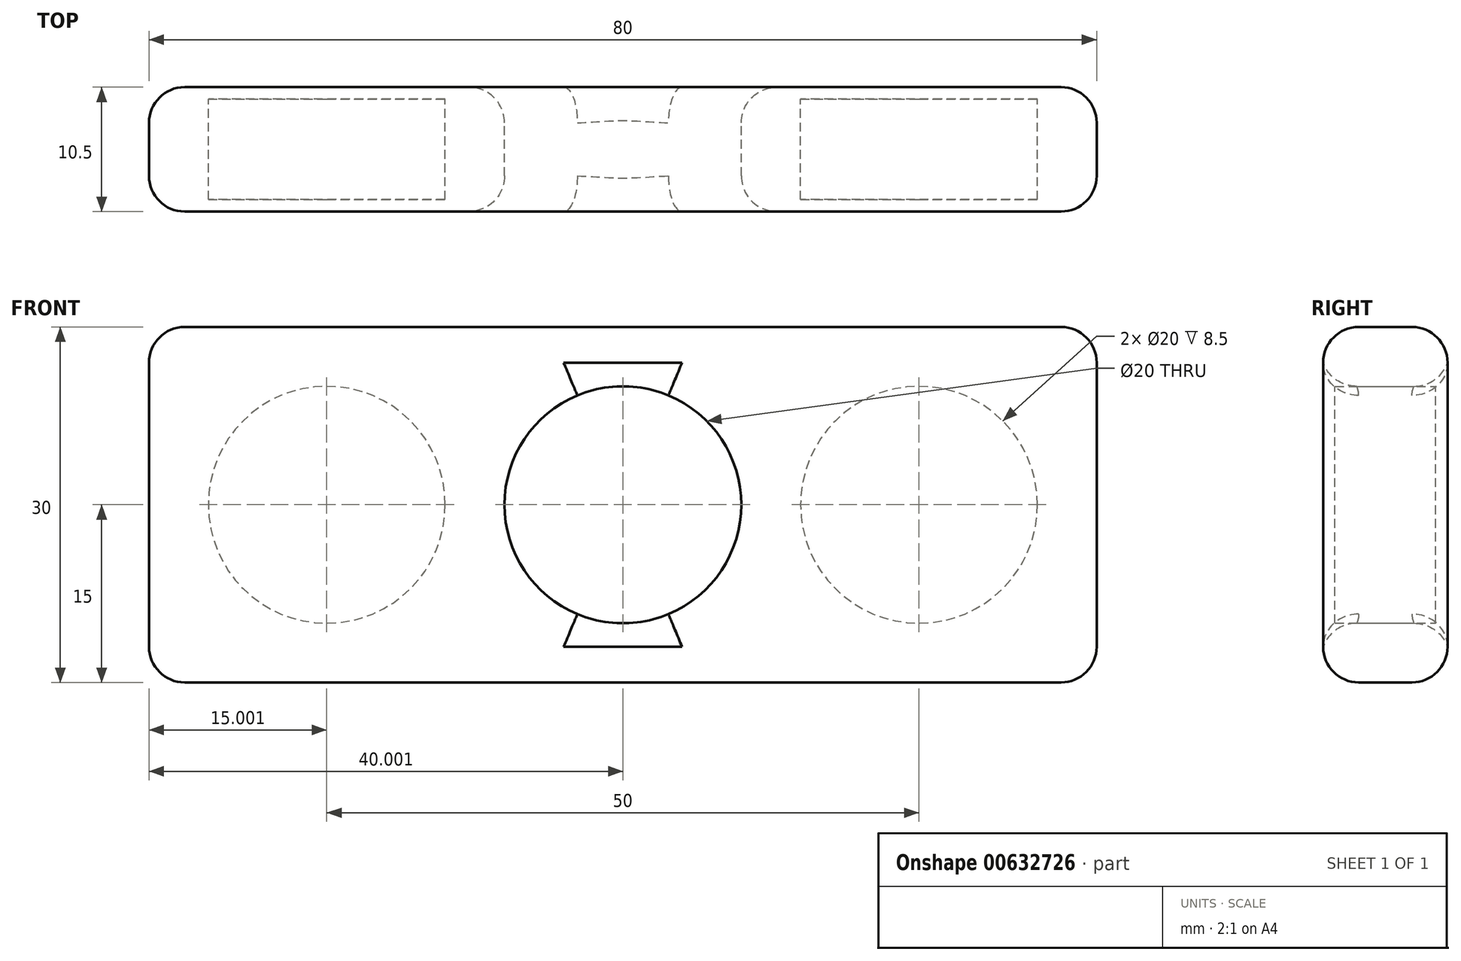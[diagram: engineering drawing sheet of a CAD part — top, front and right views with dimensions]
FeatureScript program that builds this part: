
annotation { "Feature Type Name" : "Feature", "Feature Type Description" : "" }
export const myFeature = defineFeature(function(context is Context, id is Id, definition is map)
    precondition{}
    {
        {
            var Q0;
            Q0=qCreatedBy(makeId("Front.planeOp"),FACE);
            var sketch = newSketch(context, id + "F0", { "sketchPlane" : qUnion([Q0])});
            skLineSegment(sketch, "E0.bottom", {"start": v(-23.99, 15) * mm, "end": v(-103.99, 15) * mm});
            skLineSegment(sketch, "E0.top", {"start": v(-23.99, -15) * mm, "end": v(-103.99, -15) * mm});
            skLineSegment(sketch, "E0.left", {"start": v(-23.99, 15) * mm, "end": v(-23.99, -15) * mm});
            skLineSegment(sketch, "E0.right", {"start": v(-103.99, 15) * mm, "end": v(-103.99, -15) * mm});
            skPoint(sketch, "E0.middle", {"position": v(-63.99, 0) * mm});
            skCircle(sketch, "E1", {"center": v(-63.99, 0) * mm, "radius": 10 * mm});
            skPoint(sketch, "E2.endSnap0", {"position": v(-103.99, 0) * mm});
            skCircle(sketch, "E3", {"center": v(-88.99, 0) * mm, "radius": 10 * mm});
            skCircle(sketch, "E4", {"center": v(-38.99, 0) * mm, "radius": 10 * mm});
            skSolve(sketch);
        }
        {
            var Q0;
            Q0 = qSketchRegion(id + "F0", true);
            extrude(context, id + "F1", {"entities" : qUnion([Q0]), "depth" : 8.5 * mm, "offsetDistance" : 25.4 * mm});
        }
        {
            var Q0;
            Q0=makeQuery(id+"F1.opExtrude","CAP_FACE",FACE,{"disambiguationData":[OSD([sQuery(id+"F0.wireOp",EDGE,"E0.bottom"),sQuery(id+"F0.wireOp",EDGE,"E0.top"),sQuery(id+"F0.wireOp",EDGE,"E0.left"),sQuery(id+"F0.wireOp",EDGE,"E0.right"),sQuery(id+"F0.wireOp",EDGE,"E1"),sQuery(id+"F0.wireOp",EDGE,"E3"),sQuery(id+"F0.wireOp",EDGE,"E4")])],"isStart":false});
            var sketch = newSketch(context, id + "F2", { "sketchPlane" : qUnion([Q0])});
            skLineSegment(sketch, "E5.0", {"start": v(-23.99, 15) * mm, "end": v(-103.99, 15) * mm});
            skLineSegment(sketch, "E6.0", {"start": v(-103.99, 15) * mm, "end": v(-103.99, -15) * mm});
            skLineSegment(sketch, "E7.0", {"start": v(-23.99, -15) * mm, "end": v(-103.99, -15) * mm});
            skLineSegment(sketch, "E8.0", {"start": v(-23.99, 15) * mm, "end": v(-23.99, -15) * mm});
            skCircle(sketch, "E9.0", {"center": v(-63.99, 0) * mm, "radius": 10 * mm});
            skSolve(sketch);
        }
        {
            var Q0;
            Q0 = qSketchRegion(id + "F2", true);
            extrude(context, id + "F3", {"entities" : qUnion([Q0]), "operationType" : NewBodyOperationType.ADD, "depth" : 1 * mm, "offsetDistance" : 25.4 * mm});
        }
        {
            var Q0;
            Q0=makeQuery(id+"F1.opExtrude","CAP_FACE",FACE,{"disambiguationData":[OSD([sQuery(id+"F0.wireOp",EDGE,"E0.bottom"),sQuery(id+"F0.wireOp",EDGE,"E0.top"),sQuery(id+"F0.wireOp",EDGE,"E0.left"),sQuery(id+"F0.wireOp",EDGE,"E0.right"),sQuery(id+"F0.wireOp",EDGE,"E1"),sQuery(id+"F0.wireOp",EDGE,"E3"),sQuery(id+"F0.wireOp",EDGE,"E4")])],"isStart":true});
            var sketch = newSketch(context, id + "F4", { "sketchPlane" : qUnion([Q0])});
            skLineSegment(sketch, "E10.0", {"start": v(23.99, 15) * mm, "end": v(103.99, 15) * mm});
            skLineSegment(sketch, "E11.0", {"start": v(23.99, 15) * mm, "end": v(23.99, -15) * mm});
            skLineSegment(sketch, "E12.0", {"start": v(23.99, -15) * mm, "end": v(103.99, -15) * mm});
            skLineSegment(sketch, "E13.0", {"start": v(103.99, 15) * mm, "end": v(103.99, -15) * mm});
            skCircle(sketch, "E14.0", {"center": v(63.99, 0) * mm, "radius": 10 * mm});
            skSolve(sketch);
        }
        {
            var Q0;
            Q0 = qSketchRegion(id + "F4", true);
            extrude(context, id + "F5", {"entities" : qUnion([Q0]), "operationType" : NewBodyOperationType.ADD, "depth" : 1 * mm, "offsetDistance" : 25.4 * mm});
        }
        {
            var Q0;
            Q0=makeQuery(id+"F5.opExtrude","CAP_EDGE",EDGE,{"disambiguationData":[OSD([sQuery(id+"F4.wireOp",EDGE,"E10.0")])],"isStart":false});
            var Q1;
            Q1=makeQuery(id+"F5.opExtrude","CAP_EDGE",EDGE,{"disambiguationData":[OSD([sQuery(id+"F4.wireOp",EDGE,"E11.0")])],"isStart":false});
            var Q2;
            Q2=makeQuery(id+"F5.opExtrude","CAP_EDGE",EDGE,{"disambiguationData":[OSD([sQuery(id+"F4.wireOp",EDGE,"E12.0")])],"isStart":false});
            var Q3;
            Q3=makeQuery(id+"F5.opExtrude","CAP_EDGE",EDGE,{"disambiguationData":[OSD([sQuery(id+"F4.wireOp",EDGE,"E13.0")])],"isStart":false});
            var Q4;
            Q4=makeQuery(id+"F3.opExtrude","CAP_EDGE",EDGE,{"disambiguationData":[OSD([sQuery(id+"F2.wireOp",EDGE,"E6.0")])],"isStart":false});
            var Q5;
            Q5=makeQuery(id+"F5.boolean.opBoolean","MERGE",EDGE,{"derivedFrom":[makeQuery(id+"F3.boolean.opBoolean","MERGE",EDGE,{"derivedFrom":[makeQuery(id+"F1.opExtrude","SWEPT_EDGE",EDGE,{"disambiguationData":[OSD([sQuery(id+"F0.wireOp",EDGE,"E0.top"),sQuery(id+"F0.wireOp",EDGE,"E0.right")])]}),makeQuery(id+"F3.opExtrude","SWEPT_EDGE",EDGE,{"disambiguationData":[OSD([sQuery(id+"F2.wireOp",EDGE,"E6.0"),sQuery(id+"F2.wireOp",EDGE,"E7.0")])]})]}),makeQuery(id+"F5.opExtrude","SWEPT_EDGE",EDGE,{"disambiguationData":[OSD([sQuery(id+"F4.wireOp",EDGE,"E12.0"),sQuery(id+"F4.wireOp",EDGE,"E13.0")])]})]});
            var Q6;
            Q6=makeQuery(id+"F3.opExtrude","CAP_EDGE",EDGE,{"disambiguationData":[OSD([sQuery(id+"F2.wireOp",EDGE,"E7.0")])],"isStart":false});
            var Q7;
            Q7=makeQuery(id+"F3.opExtrude","CAP_EDGE",EDGE,{"disambiguationData":[OSD([sQuery(id+"F2.wireOp",EDGE,"E5.0")])],"isStart":false});
            var Q8;
            Q8=makeQuery(id+"F5.boolean.opBoolean","MERGE",EDGE,{"derivedFrom":[makeQuery(id+"F3.boolean.opBoolean","MERGE",EDGE,{"derivedFrom":[makeQuery(id+"F1.opExtrude","SWEPT_EDGE",EDGE,{"disambiguationData":[OSD([sQuery(id+"F0.wireOp",EDGE,"E0.bottom"),sQuery(id+"F0.wireOp",EDGE,"E0.right")])]}),makeQuery(id+"F3.opExtrude","SWEPT_EDGE",EDGE,{"disambiguationData":[OSD([sQuery(id+"F2.wireOp",EDGE,"E5.0"),sQuery(id+"F2.wireOp",EDGE,"E6.0")])]})]}),makeQuery(id+"F5.opExtrude","SWEPT_EDGE",EDGE,{"disambiguationData":[OSD([sQuery(id+"F4.wireOp",EDGE,"E10.0"),sQuery(id+"F4.wireOp",EDGE,"E13.0")])]})]});
            var Q9;
            Q9=makeQuery(id+"F3.opExtrude","CAP_EDGE",EDGE,{"disambiguationData":[OSD([sQuery(id+"F2.wireOp",EDGE,"E8.0")])],"isStart":false});
            var Q10;
            Q10=makeQuery(id+"F5.boolean.opBoolean","MERGE",EDGE,{"derivedFrom":[makeQuery(id+"F3.boolean.opBoolean","MERGE",EDGE,{"derivedFrom":[makeQuery(id+"F1.opExtrude","SWEPT_EDGE",EDGE,{"disambiguationData":[OSD([sQuery(id+"F0.wireOp",EDGE,"E0.top"),sQuery(id+"F0.wireOp",EDGE,"E0.left")])]}),makeQuery(id+"F3.opExtrude","SWEPT_EDGE",EDGE,{"disambiguationData":[OSD([sQuery(id+"F2.wireOp",EDGE,"E7.0"),sQuery(id+"F2.wireOp",EDGE,"E8.0")])]})]}),makeQuery(id+"F5.opExtrude","SWEPT_EDGE",EDGE,{"disambiguationData":[OSD([sQuery(id+"F4.wireOp",EDGE,"E11.0"),sQuery(id+"F4.wireOp",EDGE,"E12.0")])]})]});
            var Q11;
            Q11=makeQuery(id+"F5.boolean.opBoolean","MERGE",EDGE,{"derivedFrom":[makeQuery(id+"F3.boolean.opBoolean","MERGE",EDGE,{"derivedFrom":[makeQuery(id+"F1.opExtrude","SWEPT_EDGE",EDGE,{"disambiguationData":[OSD([sQuery(id+"F0.wireOp",EDGE,"E0.bottom"),sQuery(id+"F0.wireOp",EDGE,"E0.left")])]}),makeQuery(id+"F3.opExtrude","SWEPT_EDGE",EDGE,{"disambiguationData":[OSD([sQuery(id+"F2.wireOp",EDGE,"E5.0"),sQuery(id+"F2.wireOp",EDGE,"E8.0")])]})]}),makeQuery(id+"F5.opExtrude","SWEPT_EDGE",EDGE,{"disambiguationData":[OSD([sQuery(id+"F4.wireOp",EDGE,"E10.0"),sQuery(id+"F4.wireOp",EDGE,"E11.0")])]})]});
            fillet(context, id + "F6", {"entities" : qUnion([Q0, Q1, Q2, Q3, Q4, Q5, Q6, Q7, Q8, Q9, Q10, Q11]), "radius" : 3 * mm, "tangentPropagation" : true, "allowEdgeOverflow" : false});
        }
        {
            var Q0;
            Q0=makeQuery(id+"F3.opExtrude","CAP_EDGE",EDGE,{"disambiguationData":[OSD([sQuery(id+"F2.wireOp",EDGE,"E9.0")])],"isStart":false});
            fillet(context, id + "F7", {"entities" : qUnion([Q0]), "radius" : 3 * mm, "tangentPropagation" : true, "allowEdgeOverflow" : false});
        }
        {
            var Q0;
            Q0=makeQuery(id+"F5.opExtrude","CAP_EDGE",EDGE,{"disambiguationData":[OSD([sQuery(id+"F4.wireOp",EDGE,"E14.0")])],"isStart":false});
            fillet(context, id + "F8", {"entities" : qUnion([Q0]), "radius" : 3 * mm, "tangentPropagation" : true, "allowEdgeOverflow" : false});
        }
    });
